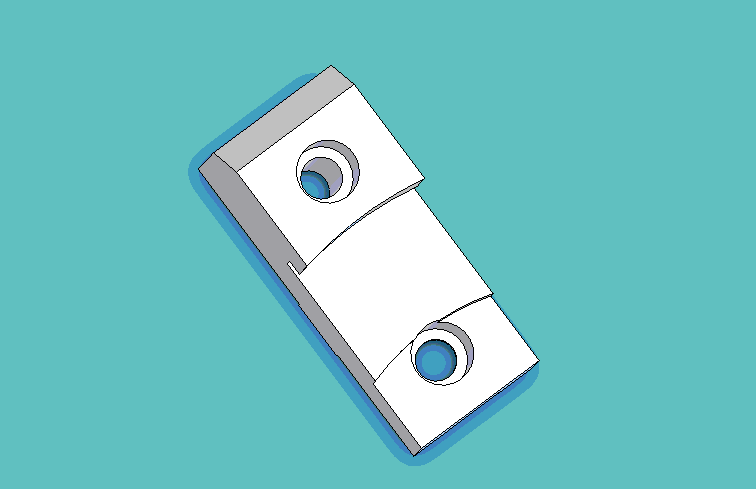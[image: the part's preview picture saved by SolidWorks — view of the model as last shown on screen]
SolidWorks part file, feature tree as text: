
SOLIDWORKS PART (.sldprt)
format: sldprt  version: not decoded by parser v0  size: 420,352 bytes
history: native  units: mm
features: sketch x12, cut_extrude x11, plane x4, material x1, extrude x1 (+10 scaffold rows collapsed)
feature tree (39):
  scaffold x10  (default folders/planes/origin — collapsed)
  material  "Material <not specified>"
  plane  "Frontal"
  plane  "Horizontal"
  plane  "Profile"
  sketch  "Sketch1"  dims[D1=1.75mm D2=4.25mm]
  extrude  "Extrude1"  Depth=2.75mm
  plane  "Plane1"
  sketch  "Sketch3"  dims[D1=0.12mm D2=2.0025mm]
  cut_extrude  "Cut-Extrude1"  Depth=2.75mm
  sketch  "Sketch4"  dims[D1=0.12mm D2=1.499mm]
  cut_extrude  "Cut-Extrude2"  Depth=2.75mm
  sketch  "Sketch5"  dims[D1=0.24mm D2=0.7515mm]
  cut_extrude  "Cut-Extrude3"  [1 undecoded]
  sketch  "Sketch6"  dims[D1=4.5mm D2=1.75mm]
  cut_extrude  "Cut-Extrude4"  Depth=1.31mm
  sketch  "Sketch7"  dims[D1=4.69mm D2=0.19mm]
  cut_extrude  "Cut-Extrude7"  Depth=0.31mm
  sketch  "Sketch8"  dims[D1=3.0mm D2=1.5mm]
  cut_extrude  "Cut-Extrude8"  Depth=0.31mm
  sketch  "Sketch11"  dims[D2=~0.502441mm D1=0.75mm]
  cut_extrude  "Cut-Extrude10"  Depth=0.81mm
  sketch  "Sketch13"  dims[D1=~0.167564mm]
  cut_extrude  "Cut-Extrude11"  Depth=0.81mm
  sketch  "Sketch14"  dims[c1.D1=~0.353736mm c1.D2=0.75mm c2.D1=2.5mm]
  cut_extrude  "Cut-Extrude12"  Depth=0.81mm
  sketch  "Sketch15"  dims[D1=~0.181876mm]
  cut_extrude  "Cut-Extrude13"  [1 undecoded]
  sketch  "Sketch16"  dims[c1.D1=0.62mm c1.D2=2.63mm c2.D2=30.0deg]
  cut_extrude  "Cut-Extrude14"  [1 undecoded]
decode coverage: 21 of 24 modeling features carry decoded parameters
note: ~ marks probable driven/reference dimensions
note: 3 parameter values undecoded
summary: no parameter record found for 3 features
note: suppression state not decoded; provenance and decode notes live in map.json
